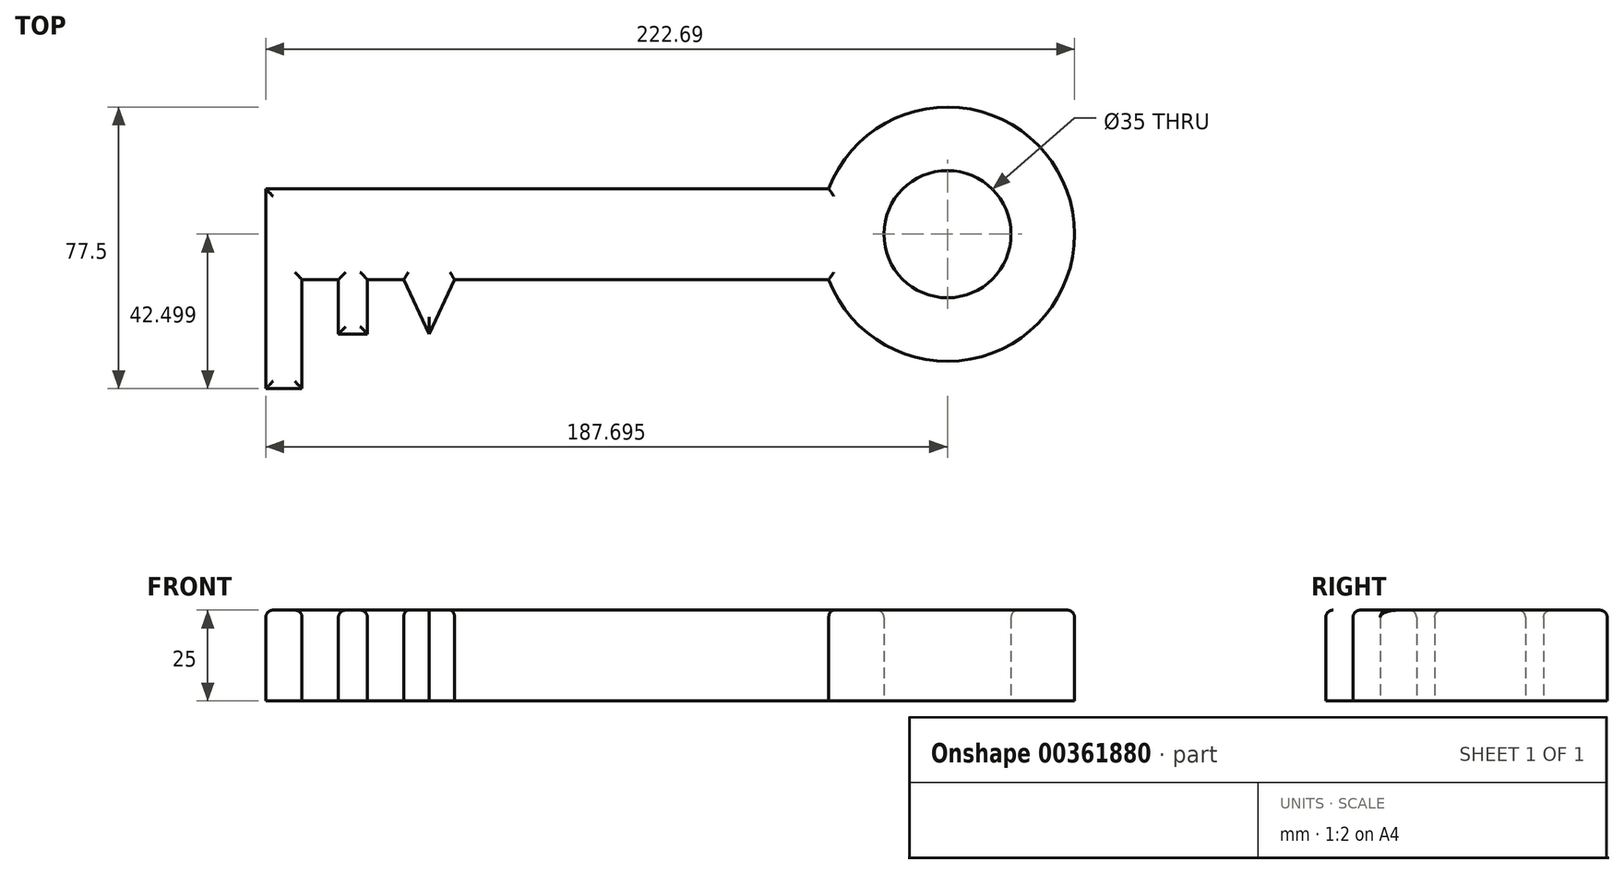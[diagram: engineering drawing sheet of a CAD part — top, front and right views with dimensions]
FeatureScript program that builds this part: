
annotation { "Feature Type Name" : "Feature", "Feature Type Description" : "" }
export const myFeature = defineFeature(function(context is Context, id is Id, definition is map)
    precondition{}
    {
        {
            var Q0;
            Q0=qCreatedBy(makeId("Top.planeOp"),FACE);
            var sketch = newSketch(context, id + "F0", { "sketchPlane" : qUnion([Q0])});
            skLineSegment(sketch, "E0.bottom", {"start": v(-72.8, 0.88) * mm, "end": v(82.2, 0.88) * mm});
            skLineSegment(sketch, "E0.top", {"start": v(-62.8, -24.12) * mm, "end": v(-52.8, -24.12) * mm});
            skLineSegment(sketch, "E0.left", {"start": v(-72.8, 0.88) * mm, "end": v(-72.8, -24.12) * mm});
            skLineSegment(sketch, "E1.top", {"start": v(-72.8, -54.12) * mm, "end": v(-62.8, -54.12) * mm});
            skLineSegment(sketch, "E1.left", {"start": v(-72.8, -24.12) * mm, "end": v(-72.8, -54.12) * mm});
            skLineSegment(sketch, "E1.right", {"start": v(-62.8, -24.12) * mm, "end": v(-62.8, -54.12) * mm});
            skLineSegment(sketch, "E2.top", {"start": v(-52.8, -39.12) * mm, "end": v(-44.8, -39.12) * mm});
            skLineSegment(sketch, "E2.left", {"start": v(-52.8, -24.12) * mm, "end": v(-52.8, -39.12) * mm});
            skLineSegment(sketch, "E2.right", {"start": v(-44.8, -24.12) * mm, "end": v(-44.8, -39.12) * mm});
            skLineSegment(sketch, "E3", {"start": v(-34.8, -24.12) * mm, "end": v(-27.8, -39.12) * mm});
            skLineSegment(sketch, "E4", {"start": v(-27.8, -39.12) * mm, "end": v(-20.8, -24.12) * mm});
            skArc(sketch, "E5", {"start": v(82.2, -24.12) * mm, "mid": v(149.9, -11.62) * mm, "end": v(82.2, 0.88) * mm});
            skCircle(sketch, "E6", {"center": v(114.9, -11.62) * mm, "radius": 17.5 * mm});
            skLineSegment(sketch, "E7.trimOffspring", {"start": v(-44.8, -24.12) * mm, "end": v(82.2, -24.12) * mm});
            skSolve(sketch);
        }
        {
            var Q0;
            Q0=makeQuery(id+"F0.imprint","IMPRINT",FACE,{"disambiguationData":[TD([[makeQuery(id+"F0.imprint","IMPRINT",EDGE,{"derivedFrom":sQuery(id+"F0.wireOp",EDGE,"E0.bottom")}),-1.0]])]});
            var Q1;
            {var subQ0=sQuery(id+"F0.wireOp",EDGE,"E3");Q1=makeQuery(id+"F0.imprint","IMPRINT",FACE,{"disambiguationData":[TD([[makeQuery(id+"F0.imprint","IMPRINT",EDGE,{"derivedFrom":subQ0}),1.0]])]});}
            extrude(context, id + "F1", {"entities" : qUnion([Q0, Q1]), "depth" : 25 * mm});
        }
        {
            var Q0;
            Q0=makeQuery(id+"F1.opExtrude","CAP_FACE",FACE,{"disambiguationData":[OSD([sQuery(id+"F0.wireOp",EDGE,"E0.bottom"),sQuery(id+"F0.wireOp",EDGE,"E0.top"),sQuery(id+"F0.wireOp",EDGE,"E0.left"),sQuery(id+"F0.wireOp",EDGE,"E1.top"),sQuery(id+"F0.wireOp",EDGE,"E1.left"),sQuery(id+"F0.wireOp",EDGE,"E1.right"),sQuery(id+"F0.wireOp",EDGE,"E2.top"),sQuery(id+"F0.wireOp",EDGE,"E2.left"),sQuery(id+"F0.wireOp",EDGE,"E2.right"),sQuery(id+"F0.wireOp",EDGE,"E3"),sQuery(id+"F0.wireOp",EDGE,"E4"),sQuery(id+"F0.wireOp",EDGE,"E5"),sQuery(id+"F0.wireOp",EDGE,"E6"),sQuery(id+"F0.wireOp",EDGE,"E7.trimOffspring")])],"isStart":false});
            fillet(context, id + "F2", {"entities" : qUnion([Q0]), "radius" : 2 * mm, "tangentPropagation" : true, "allowEdgeOverflow" : false});
        }
    });
